# Revit family: _JohansonDesign_Chair_Frankie 08-46
name_source: partatom
category: Мебель
revit_build: Autodesk Revit 2017 (Build: 20160225_1515(x64)
units: mm (PartAtom-declared; Revit-internal decimal feet)

## family parameters
Всегда вертикально = Да
Заголовок OmniClass = Chairs
На основе рабочей плоскости = Нет
Номер OmniClass = 23.40.20.14.14.11
Общий = Нет
При загрузке вырезать с полостями = Нет
Точка расчета площади = Нет

## types (2) — shared parameters
AssetType = Movable
Brand = Johanson Design
Category = Chairs
Collection = Frankie
Color = Various
Designer = Fredrik Färg & Emma Blanche
DurationUnit = Year
ExpiringDate = 07/2018
Finish = Chrome / multicolour
HighestSeatingHeight = 460 мм
IfcExportAs = IfcFurnishingElementType
IfcExportType = CHAIR
LowestSeatingHeight = 460 мм
ManufacturerName = Johanson Design
ManufacturerURL = http://johansondesign.com
Material = Metal + fabric/leather
MaterialsURL = http://johansondesign.com
NBSDescription = Domestic chairs
NBSReference = 45-35-20/365
Name = Chair_Frankie
NominalDepth = 480 мм
NominalHeight = 815 мм
NominalWidth = 460 мм
ProductInformation = Created for oﬃces and commercial environments
SeatingHeight = 460 мм
Shape = Sculptured
Size = 460x480x815 mm
Style = Modern, scandinavian
Uniclass2 = Pr_40_50_12_48
Uniclass2015Description = Dining chairs
Uniclass2015Reference = Pr_40_50_12_22
Version = 1
VersionDate = 09/10/2017
WarrantyDurationUnit = Year
Изготовитель = Johanson Design
Описание = Created for oﬃces and commercial environments
zero-valued in all types: Стоимость

## per-type parameters (varying)
| type | ConvergoRefNr | URL |
| Frankie 08-46 | 0116-1709-0005-SE | http://johansondesign.com |
| Frankie 09-46 | 0116-1709-0006-SE | http://file-system.ru |

note: column(s) folded — value = type name in every type: ChairType, Группа модели

## geometry (parser evidence)
native form markers: Blend x4, Sweep x7
no freeform markers — native parametric forms only
